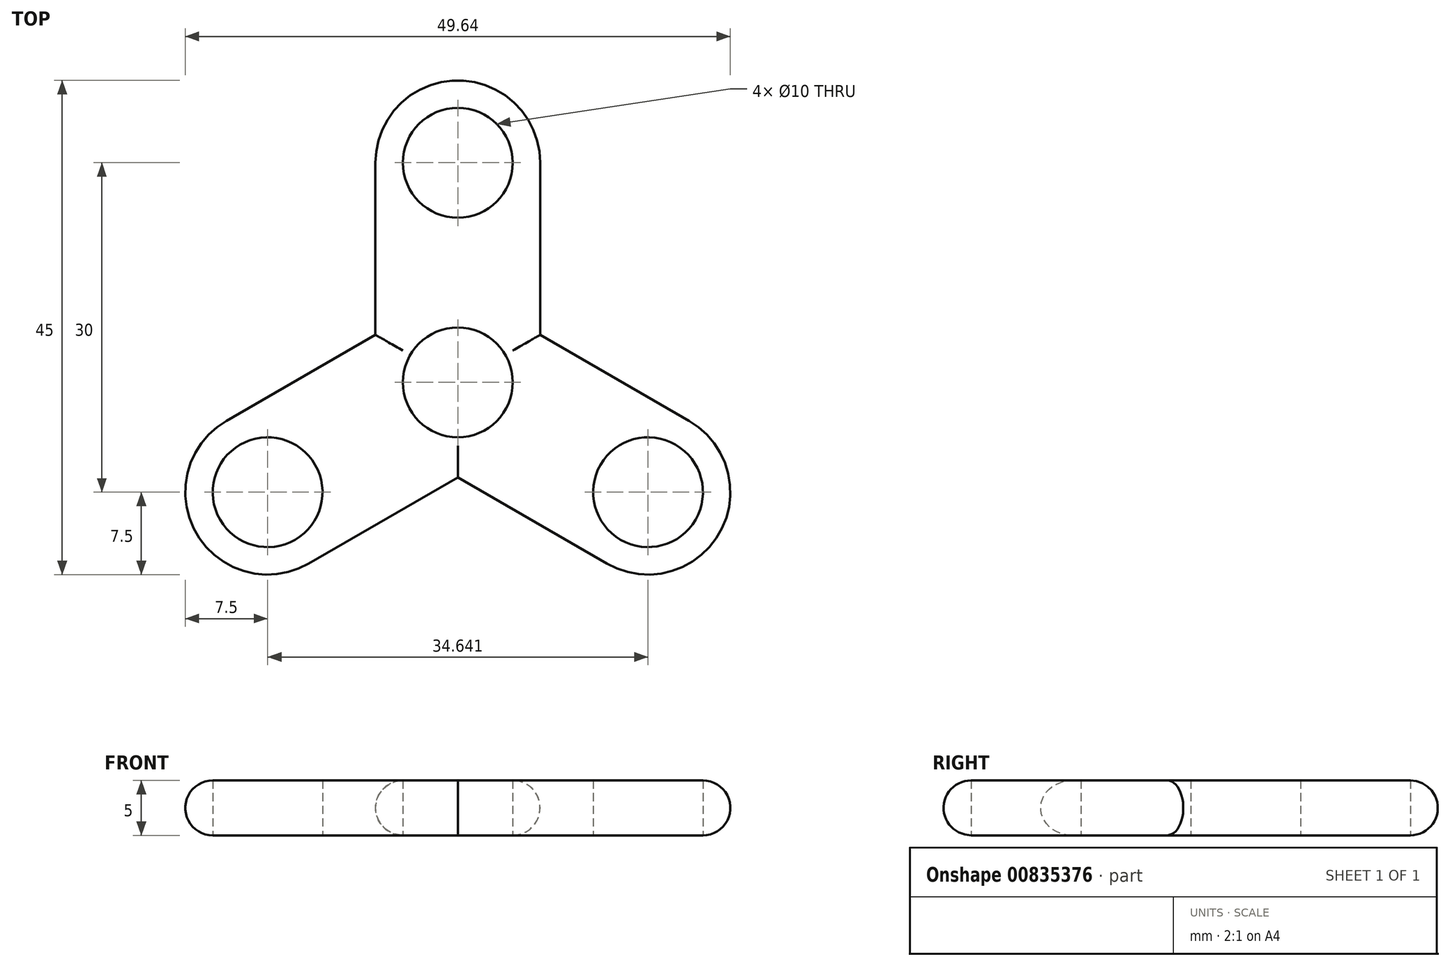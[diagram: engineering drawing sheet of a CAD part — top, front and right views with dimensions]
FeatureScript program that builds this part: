
annotation { "Feature Type Name" : "Feature", "Feature Type Description" : "" }
export const myFeature = defineFeature(function(context is Context, id is Id, definition is map)
    precondition{}
    {
        {
            var Q0;
            Q0=qCreatedBy(makeId("Top.planeOp"),FACE);
            var sketch = newSketch(context, id + "F0", { "sketchPlane" : qUnion([Q0])});
            skCircle(sketch, "E0", {"center": v(0, 0) * mm, "radius": 7.5 * mm});
            skLineSegment(sketch, "E1", {"start": v(0, 0) * mm, "end": v(0, 20) * mm});
            skCircle(sketch, "E2", {"center": v(0, 20) * mm, "radius": 7.5 * mm});
            skLineSegment(sketch, "E3", {"start": v(0, 0) * mm, "end": v(-7.5, 0) * mm});
            skLineSegment(sketch, "E4", {"start": v(0, 10) * mm, "end": v(-6, 10) * mm});
            skCircle(sketch, "E5", {"center": v(0, 20) * mm, "radius": 5 * mm});
            skCircle(sketch, "E6", {"center": v(0, 0) * mm, "radius": 5 * mm});
            skLineSegment(sketch, "E7.MirrorCS", {"start": v(0, 20) * mm, "end": v(-7.5, 20) * mm});
            skLineSegment(sketch, "E8.MirrorCS", {"start": v(0, 20) * mm, "end": v(7.5, 20) * mm});
            skLineSegment(sketch, "E9.MirrorCS", {"start": v(0, 0) * mm, "end": v(7.5, 0) * mm});
            skLineSegment(sketch, "E10", {"start": v(-7.5, 20) * mm, "end": v(-7.5, 0) * mm});
            skLineSegment(sketch, "E11", {"start": v(7.5, 0) * mm, "end": v(7.5, 20) * mm});
            skCircle(sketch, "E12.1.0", {"center": v(-17.32, -10) * mm, "radius": 5 * mm});
            skCircle(sketch, "E12.1.1", {"center": v(-17.32, -10) * mm, "radius": 7.5 * mm});
            skLineSegment(sketch, "E12.1.2", {"start": v(-13.57, -16.5) * mm, "end": v(3.75, -6.5) * mm});
            skLineSegment(sketch, "E12.1.3", {"start": v(-3.75, 6.5) * mm, "end": v(-21.07, -3.5) * mm});
            skCircle(sketch, "E12.2.0", {"center": v(17.32, -10) * mm, "radius": 5 * mm});
            skCircle(sketch, "E12.2.1", {"center": v(17.32, -10) * mm, "radius": 7.5 * mm});
            skLineSegment(sketch, "E12.2.2", {"start": v(21.07, -3.5) * mm, "end": v(3.75, 6.5) * mm});
            skLineSegment(sketch, "E12.2.3", {"start": v(-3.75, -6.5) * mm, "end": v(13.57, -16.5) * mm});
            skSolve(sketch);
        }
        {
            var Q0;
            Q0 = qSketchRegion(id + "F0", true);
            var Q1;
            {var subQ1=sQuery(id+"F0.wireOp",EDGE,"E0");var subQ7=makeQuery(id+"F0.imprint","INTERSECT",VERTEX,{"derivedFrom":[subQ1,sQuery(id+"F0.wireOp",EDGE,"E12.1.3")]});Q1=makeQuery(id+"F0.imprint","IMPRINT",FACE,{"disambiguationData":[TD([[makeQuery(id+"F0.imprint","IMPRINT",EDGE,{"disambiguationData":[TD([[subQ7,1.0]])],"derivedFrom":subQ1}),1.0]])]});}
            var Q2;
            {var subQ1=sQuery(id+"F0.wireOp",EDGE,"E0");var subQ7=makeQuery(id+"F0.imprint","INTERSECT",VERTEX,{"derivedFrom":[subQ1,sQuery(id+"F0.wireOp",EDGE,"E12.1.2")]});Q2=makeQuery(id+"F0.imprint","IMPRINT",FACE,{"disambiguationData":[TD([[makeQuery(id+"F0.imprint","IMPRINT",EDGE,{"disambiguationData":[TD([[subQ7,1.0]])],"derivedFrom":subQ1}),1.0]])]});}
            var Q3;
            {var subQ1=sQuery(id+"F0.wireOp",EDGE,"E0");var subQ7=makeQuery(id+"F0.imprint","INTERSECT",VERTEX,{"derivedFrom":[subQ1,sQuery(id+"F0.wireOp",EDGE,"E12.2.2")]});Q3=makeQuery(id+"F0.imprint","IMPRINT",FACE,{"disambiguationData":[TD([[makeQuery(id+"F0.imprint","IMPRINT",EDGE,{"disambiguationData":[TD([[subQ7,-1.0]])],"derivedFrom":subQ1}),1.0]])]});}
            extrude(context, id + "F1", {"entities" : qUnion([Q0, Q1, Q2, Q3]), "depth" : 5 * mm, "offsetDistance" : 25 * mm});
        }
        {
            var Q0;
            Q0=makeQuery(id+"F1.opExtrude","CAP_EDGE",EDGE,{"disambiguationData":[OSD([sQuery(id+"F0.wireOp",EDGE,"E10")])],"isStart":false});
            var Q1;
            Q1=makeQuery(id+"F1.opExtrude","CAP_EDGE",EDGE,{"disambiguationData":[OSD([sQuery(id+"F0.wireOp",EDGE,"E12.1.3")])],"isStart":false});
            var Q2;
            Q2=makeQuery(id+"F1.opExtrude","CAP_EDGE",EDGE,{"disambiguationData":[OSD([sQuery(id+"F0.wireOp",EDGE,"E12.2.3")])],"isStart":false});
            var Q3;
            Q3=makeQuery(id+"F1.opExtrude","CAP_EDGE",EDGE,{"disambiguationData":[OSD([sQuery(id+"F0.wireOp",EDGE,"E12.1.2")])],"isStart":true});
            var Q4;
            Q4=makeQuery(id+"F1.opExtrude","CAP_EDGE",EDGE,{"disambiguationData":[OSD([sQuery(id+"F0.wireOp",EDGE,"E12.2.3")])],"isStart":true});
            var Q5;
            Q5=makeQuery(id+"F1.opExtrude","CAP_EDGE",EDGE,{"disambiguationData":[OSD([sQuery(id+"F0.wireOp",EDGE,"E11")])],"isStart":true});
            fillet(context, id + "F2", {"entities" : qUnion([Q0, Q1, Q2, Q3, Q4, Q5]), "radius" : 2.5 * mm, "tangentPropagation" : true, "allowEdgeOverflow" : false});
        }
    });
